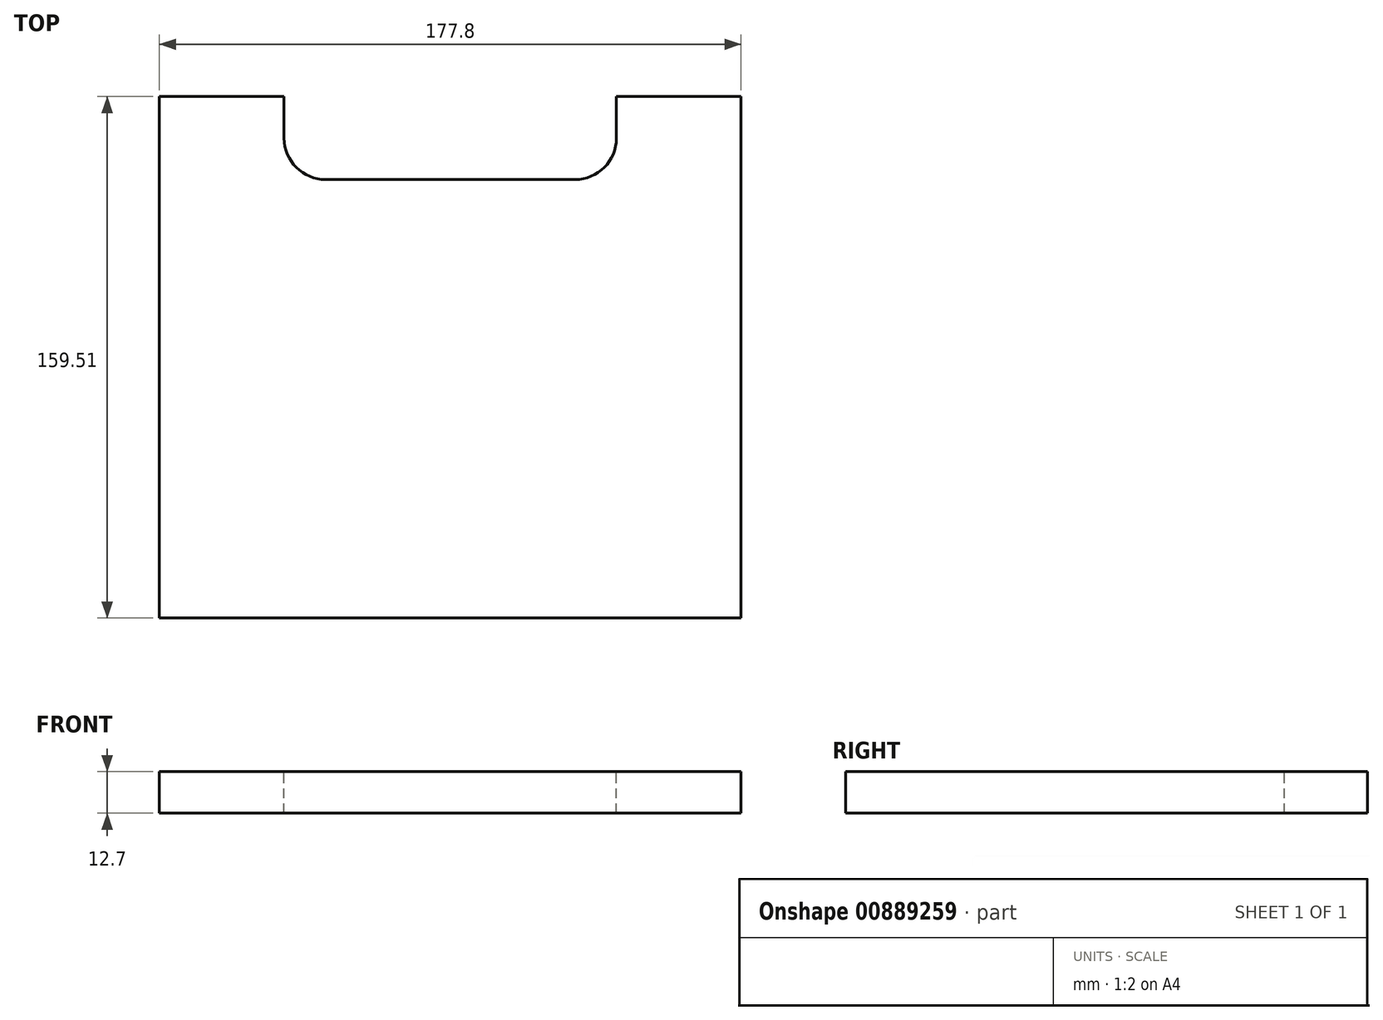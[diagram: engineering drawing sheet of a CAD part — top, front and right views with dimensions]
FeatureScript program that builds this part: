
annotation { "Feature Type Name" : "Feature", "Feature Type Description" : "" }
export const myFeature = defineFeature(function(context is Context, id is Id, definition is map)
    precondition{}
    {
        {
            var Q0;
            Q0=qCreatedBy(makeId("Top.planeOp"),FACE);
            var sketch = newSketch(context, id + "F0", { "sketchPlane" : qUnion([Q0])});
            skLineSegment(sketch, "E0.bottom", {"start": v(0, 0) * mm, "end": v(177.8, 0) * mm});
            skLineSegment(sketch, "E0.top", {"start": v(0, 159.51) * mm, "end": v(177.8, 159.51) * mm});
            skLineSegment(sketch, "E0.left", {"start": v(0, 0) * mm, "end": v(0, 159.51) * mm});
            skLineSegment(sketch, "E0.right", {"start": v(177.8, 0) * mm, "end": v(177.8, 159.51) * mm});
            skSolve(sketch);
        }
        {
            var Q0;
            Q0 = qSketchRegion(id + "F0", true);
            extrude(context, id + "F1", {"entities" : qUnion([Q0]), "depth" : 12.7 * mm, "offsetDistance" : 25.4 * mm});
        }
        {
            var Q0;
            Q0=makeQuery(id+"F1.opExtrude","CAP_FACE",FACE,{"disambiguationData":[OSD([sQuery(id+"F0.wireOp",EDGE,"E0.bottom"),sQuery(id+"F0.wireOp",EDGE,"E0.top"),sQuery(id+"F0.wireOp",EDGE,"E0.left"),sQuery(id+"F0.wireOp",EDGE,"E0.right")])],"isStart":false});
            var sketch = newSketch(context, id + "F2", { "sketchPlane" : qUnion([Q0])});
            skLineSegment(sketch, "E1.bottom", {"start": v(38.1, 159.51) * mm, "end": v(139.7, 159.51) * mm});
            skLineSegment(sketch, "E1.top", {"start": v(50.8, 134.11) * mm, "end": v(127, 134.11) * mm});
            skLineSegment(sketch, "E1.left", {"start": v(38.1, 159.51) * mm, "end": v(38.1, 146.81) * mm});
            skLineSegment(sketch, "E1.right", {"start": v(139.7, 159.51) * mm, "end": v(139.7, 146.81) * mm});
            skLineSegment(sketch, "E2", {"start": v(88.9, 0) * mm, "end": v(88.9, 134.11) * mm});
            skPoint(sketch, "E3.visualSharp", {"position": v(38.1, 134.11) * mm});
            skArc(sketch, "E3.filletArc", {"start": v(38.1, 146.81) * mm, "mid": v(41.82, 137.83) * mm, "end": v(50.8, 134.11) * mm});
            skPoint(sketch, "E4.visualSharp", {"position": v(139.7, 134.11) * mm});
            skArc(sketch, "E4.filletArc", {"start": v(127, 134.11) * mm, "mid": v(135.98, 137.83) * mm, "end": v(139.7, 146.81) * mm});
            skSolve(sketch);
        }
        {
            var Q0;
            Q0 = qSketchRegion(id + "F2", true);
            extrude(context, id + "F3", {"entities" : qUnion([Q0]), "operationType" : NewBodyOperationType.REMOVE, "endBound" : BoundingType.THROUGH_ALL, "oppositeDirection" : true, "depth" : 25.4 * mm, "offsetDistance" : 25.4 * mm});
        }
    });
